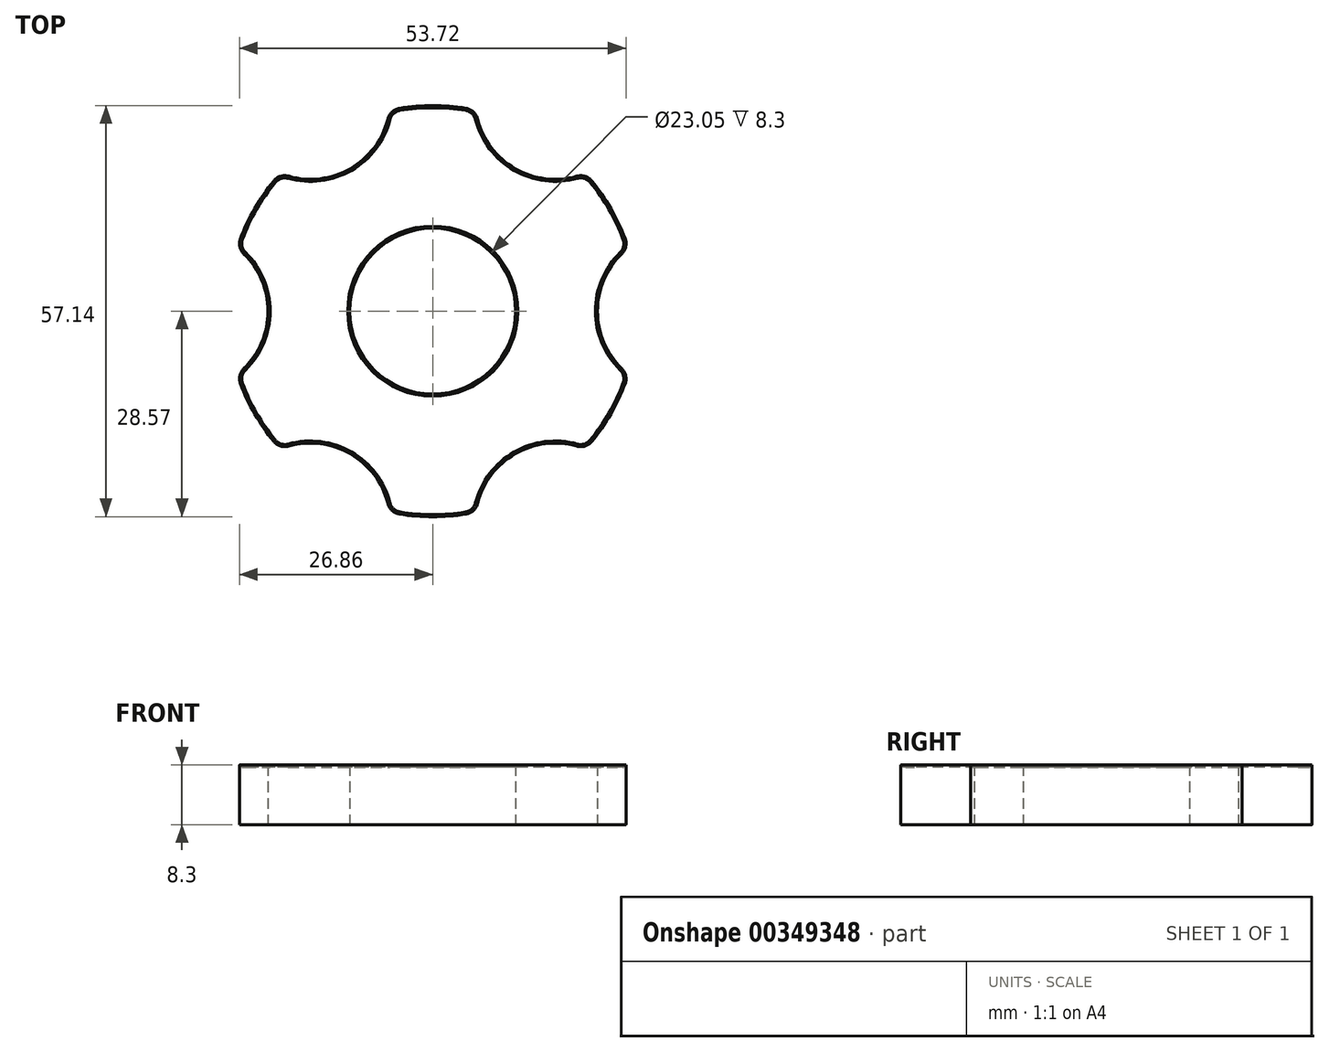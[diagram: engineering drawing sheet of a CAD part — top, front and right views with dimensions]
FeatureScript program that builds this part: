
annotation { "Feature Type Name" : "Feature", "Feature Type Description" : "" }
export const myFeature = defineFeature(function(context is Context, id is Id, definition is map)
    precondition{}
    {
        {
            var Q0;
            Q0=qCreatedBy(makeId("Top.planeOp"),FACE);
            var sketch = newSketch(context, id + "F0", { "sketchPlane" : qUnion([Q0])});
            skCircle(sketch, "E0", {"center": v(0, 0) * mm, "radius": 28.58 * mm});
            skCircle(sketch, "E1", {"center": v(0, 0) * mm, "radius": 11.53 * mm});
            skSolve(sketch);
        }
        {
            var Q0;
            Q0=makeQuery(id+"F0.imprint","IMPRINT",FACE,{"disambiguationData":[TD([[makeQuery(id+"F0.imprint","IMPRINT",EDGE,{"derivedFrom":sQuery(id+"F0.wireOp",EDGE,"E0")}),1.0]])]});
            extrude(context, id + "F1", {"entities" : qUnion([Q0]), "depth" : 8 * mm, "offsetDistance" : 25 * mm});
        }
        {
            var Q0;
            Q0=qCreatedBy(makeId("Top.planeOp"),FACE);
            var sketch = newSketch(context, id + "F2", { "sketchPlane" : qUnion([Q0])});
            skCircle(sketch, "E2", {"center": v(0, 0) * mm, "radius": 34.01 * mm});
            skCircle(sketch, "E3", {"center": v(-34.01, 0) * mm, "radius": 11.11 * mm});
            skCircle(sketch, "E4.1.0", {"center": v(-17, -29.45) * mm, "radius": 11.11 * mm});
            skCircle(sketch, "E4.2.0", {"center": v(17, -29.45) * mm, "radius": 11.11 * mm});
            skCircle(sketch, "E4.3.0", {"center": v(34.01, 0) * mm, "radius": 11.11 * mm});
            skCircle(sketch, "E4.4.0", {"center": v(17, 29.45) * mm, "radius": 11.11 * mm});
            skCircle(sketch, "E4.5.0", {"center": v(-17, 29.45) * mm, "radius": 11.11 * mm});
            skSolve(sketch);
        }
        {
            var Q0;
            {var subQ0=sQuery(id+"F2.wireOp",EDGE,"E4.2.0");var subQ1=sQuery(id+"F2.wireOp",EDGE,"E2");var subQ2=makeQuery(id+"F2.imprint","INTERSECT",VERTEX,{"disambiguationData":[OD(0.0)],"derivedFrom":[subQ1,subQ0]});Q0=makeQuery(id+"F2.imprint","IMPRINT",FACE,{"disambiguationData":[TD([[makeQuery(id+"F2.imprint","IMPRINT",EDGE,{"disambiguationData":[TD([[subQ2,-1.0]])],"derivedFrom":subQ1}),1.0]])]});}
            var Q1;
            {var subQ0=sQuery(id+"F2.wireOp",EDGE,"E4.1.0");var subQ1=sQuery(id+"F2.wireOp",EDGE,"E2");var subQ2=makeQuery(id+"F2.imprint","INTERSECT",VERTEX,{"disambiguationData":[OD(0.0)],"derivedFrom":[subQ1,subQ0]});Q1=makeQuery(id+"F2.imprint","IMPRINT",FACE,{"disambiguationData":[TD([[makeQuery(id+"F2.imprint","IMPRINT",EDGE,{"disambiguationData":[TD([[subQ2,-1.0]])],"derivedFrom":subQ1}),1.0]])]});}
            var Q2;
            {var subQ0=sQuery(id+"F2.wireOp",EDGE,"E3");var subQ1=sQuery(id+"F2.wireOp",EDGE,"E2");var subQ2=makeQuery(id+"F2.imprint","INTERSECT",VERTEX,{"disambiguationData":[OD(0.0)],"derivedFrom":[subQ1,subQ0]});Q2=makeQuery(id+"F2.imprint","IMPRINT",FACE,{"disambiguationData":[TD([[makeQuery(id+"F2.imprint","IMPRINT",EDGE,{"disambiguationData":[TD([[subQ2,-1.0]])],"derivedFrom":subQ1}),1.0]])]});}
            var Q3;
            {var subQ0=sQuery(id+"F2.wireOp",EDGE,"E4.5.0");var subQ1=sQuery(id+"F2.wireOp",EDGE,"E2");var subQ2=makeQuery(id+"F2.imprint","INTERSECT",VERTEX,{"disambiguationData":[OD(0.0)],"derivedFrom":[subQ1,subQ0]});Q3=makeQuery(id+"F2.imprint","IMPRINT",FACE,{"disambiguationData":[TD([[makeQuery(id+"F2.imprint","IMPRINT",EDGE,{"disambiguationData":[TD([[subQ2,-1.0]])],"derivedFrom":subQ1}),1.0]])]});}
            var Q4;
            {var subQ0=sQuery(id+"F2.wireOp",EDGE,"E4.4.0");var subQ1=sQuery(id+"F2.wireOp",EDGE,"E2");var subQ2=makeQuery(id+"F2.imprint","INTERSECT",VERTEX,{"disambiguationData":[OD(0.0)],"derivedFrom":[subQ1,subQ0]});Q4=makeQuery(id+"F2.imprint","IMPRINT",FACE,{"disambiguationData":[TD([[makeQuery(id+"F2.imprint","IMPRINT",EDGE,{"disambiguationData":[TD([[subQ2,-1.0]])],"derivedFrom":subQ1}),1.0]])]});}
            var Q5;
            {var subQ0=sQuery(id+"F2.wireOp",EDGE,"E4.3.0");var subQ1=sQuery(id+"F2.wireOp",EDGE,"E2");var subQ2=makeQuery(id+"F2.imprint","INTERSECT",VERTEX,{"disambiguationData":[OD(0.0)],"derivedFrom":[subQ1,subQ0]});Q5=makeQuery(id+"F2.imprint","IMPRINT",FACE,{"disambiguationData":[TD([[makeQuery(id+"F2.imprint","IMPRINT",EDGE,{"disambiguationData":[TD([[subQ2,1.0]])],"derivedFrom":subQ1}),1.0]])]});}
            extrude(context, id + "F3", {"entities" : qUnion([Q0, Q1, Q2, Q3, Q4, Q5]), "operationType" : NewBodyOperationType.REMOVE, "depth" : 25.4 * mm});
        }
        {
            var Q0;
            Q0=qCreatedBy(makeId("Top.planeOp"),FACE);
            var sketch = newSketch(context, id + "F4", { "sketchPlane" : qUnion([Q0])});
            skCircle(sketch, "E5", {"center": v(0, 22.86) * mm, "radius": 2.38 * mm});
            skCircle(sketch, "E6.1.0", {"center": v(-19.8, 11.43) * mm, "radius": 2.38 * mm});
            skCircle(sketch, "E6.2.0", {"center": v(-19.8, -11.43) * mm, "radius": 2.38 * mm});
            skCircle(sketch, "E6.3.0", {"center": v(0, -22.86) * mm, "radius": 2.38 * mm});
            skCircle(sketch, "E6.4.0", {"center": v(19.8, -11.43) * mm, "radius": 2.38 * mm});
            skCircle(sketch, "E6.5.0", {"center": v(19.8, 11.43) * mm, "radius": 2.38 * mm});
            skPoint(sketch, "E6.center", {"position": v(0, 0) * mm});
            skSolve(sketch);
        }
        {
            var Q0;
            Q0=makeQuery(id+"F3.boolean.opBoolean","INTERSECT",EDGE,{"disambiguationData":[OD(0.0)],"derivedFrom":[makeQuery(id+"F1.opExtrude","SWEPT_FACE",FACE,{"disambiguationData":[OSD([sQuery(id+"F0.wireOp",EDGE,"E0")])]}),makeQuery(id+"F3.opExtrude","SWEPT_FACE",FACE,{"disambiguationData":[OSD([sQuery(id+"F2.wireOp",EDGE,"E4.1.0")])]})]});
            var Q1;
            Q1=makeQuery(id+"F3.boolean.opBoolean","INTERSECT",EDGE,{"disambiguationData":[OD(0.0)],"derivedFrom":[makeQuery(id+"F1.opExtrude","SWEPT_FACE",FACE,{"disambiguationData":[OSD([sQuery(id+"F0.wireOp",EDGE,"E0")])]}),makeQuery(id+"F3.opExtrude","SWEPT_FACE",FACE,{"disambiguationData":[OSD([sQuery(id+"F2.wireOp",EDGE,"E3")])]})]});
            var Q2;
            Q2=makeQuery(id+"F3.boolean.opBoolean","INTERSECT",EDGE,{"disambiguationData":[OD(1.0)],"derivedFrom":[makeQuery(id+"F1.opExtrude","SWEPT_FACE",FACE,{"disambiguationData":[OSD([sQuery(id+"F0.wireOp",EDGE,"E0")])]}),makeQuery(id+"F3.opExtrude","SWEPT_FACE",FACE,{"disambiguationData":[OSD([sQuery(id+"F2.wireOp",EDGE,"E3")])]})]});
            var Q3;
            Q3=makeQuery(id+"F3.boolean.opBoolean","INTERSECT",EDGE,{"disambiguationData":[OD(0.0)],"derivedFrom":[makeQuery(id+"F1.opExtrude","SWEPT_FACE",FACE,{"disambiguationData":[OSD([sQuery(id+"F0.wireOp",EDGE,"E0")])]}),makeQuery(id+"F3.opExtrude","SWEPT_FACE",FACE,{"disambiguationData":[OSD([sQuery(id+"F2.wireOp",EDGE,"E4.5.0")])]})]});
            var Q4;
            Q4=makeQuery(id+"F3.boolean.opBoolean","INTERSECT",EDGE,{"disambiguationData":[OD(1.0)],"derivedFrom":[makeQuery(id+"F1.opExtrude","SWEPT_FACE",FACE,{"disambiguationData":[OSD([sQuery(id+"F0.wireOp",EDGE,"E0")])]}),makeQuery(id+"F3.opExtrude","SWEPT_FACE",FACE,{"disambiguationData":[OSD([sQuery(id+"F2.wireOp",EDGE,"E4.5.0")])]})]});
            var Q5;
            Q5=makeQuery(id+"F3.boolean.opBoolean","INTERSECT",EDGE,{"disambiguationData":[OD(1.0)],"derivedFrom":[makeQuery(id+"F1.opExtrude","SWEPT_FACE",FACE,{"disambiguationData":[OSD([sQuery(id+"F0.wireOp",EDGE,"E0")])]}),makeQuery(id+"F3.opExtrude","SWEPT_FACE",FACE,{"disambiguationData":[OSD([sQuery(id+"F2.wireOp",EDGE,"E4.4.0")])]})]});
            var Q6;
            Q6=makeQuery(id+"F3.boolean.opBoolean","INTERSECT",EDGE,{"disambiguationData":[OD(0.0)],"derivedFrom":[makeQuery(id+"F1.opExtrude","SWEPT_FACE",FACE,{"disambiguationData":[OSD([sQuery(id+"F0.wireOp",EDGE,"E0")])]}),makeQuery(id+"F3.opExtrude","SWEPT_FACE",FACE,{"disambiguationData":[OSD([sQuery(id+"F2.wireOp",EDGE,"E4.4.0")])]})]});
            var Q7;
            Q7=makeQuery(id+"F3.boolean.opBoolean","INTERSECT",EDGE,{"disambiguationData":[OD(1.0)],"derivedFrom":[makeQuery(id+"F1.opExtrude","SWEPT_FACE",FACE,{"disambiguationData":[OSD([sQuery(id+"F0.wireOp",EDGE,"E0")])]}),makeQuery(id+"F3.opExtrude","SWEPT_FACE",FACE,{"disambiguationData":[OSD([sQuery(id+"F2.wireOp",EDGE,"E4.3.0")])]})]});
            var Q8;
            Q8=makeQuery(id+"F3.boolean.opBoolean","INTERSECT",EDGE,{"disambiguationData":[OD(0.0)],"derivedFrom":[makeQuery(id+"F1.opExtrude","SWEPT_FACE",FACE,{"disambiguationData":[OSD([sQuery(id+"F0.wireOp",EDGE,"E0")])]}),makeQuery(id+"F3.opExtrude","SWEPT_FACE",FACE,{"disambiguationData":[OSD([sQuery(id+"F2.wireOp",EDGE,"E4.3.0")])]})]});
            var Q9;
            Q9=makeQuery(id+"F3.boolean.opBoolean","INTERSECT",EDGE,{"disambiguationData":[OD(1.0)],"derivedFrom":[makeQuery(id+"F1.opExtrude","SWEPT_FACE",FACE,{"disambiguationData":[OSD([sQuery(id+"F0.wireOp",EDGE,"E0")])]}),makeQuery(id+"F3.opExtrude","SWEPT_FACE",FACE,{"disambiguationData":[OSD([sQuery(id+"F2.wireOp",EDGE,"E4.2.0")])]})]});
            var Q10;
            Q10=makeQuery(id+"F3.boolean.opBoolean","INTERSECT",EDGE,{"disambiguationData":[OD(0.0)],"derivedFrom":[makeQuery(id+"F1.opExtrude","SWEPT_FACE",FACE,{"disambiguationData":[OSD([sQuery(id+"F0.wireOp",EDGE,"E0")])]}),makeQuery(id+"F3.opExtrude","SWEPT_FACE",FACE,{"disambiguationData":[OSD([sQuery(id+"F2.wireOp",EDGE,"E4.2.0")])]})]});
            var Q11;
            Q11=makeQuery(id+"F3.boolean.opBoolean","INTERSECT",EDGE,{"disambiguationData":[OD(1.0)],"derivedFrom":[makeQuery(id+"F1.opExtrude","SWEPT_FACE",FACE,{"disambiguationData":[OSD([sQuery(id+"F0.wireOp",EDGE,"E0")])]}),makeQuery(id+"F3.opExtrude","SWEPT_FACE",FACE,{"disambiguationData":[OSD([sQuery(id+"F2.wireOp",EDGE,"E4.1.0")])]})]});
            fillet(context, id + "F5", {"entities" : qUnion([Q0, Q1, Q2, Q3, Q4, Q5, Q6, Q7, Q8, Q9, Q10, Q11]), "radius" : 2 * mm, "tangentPropagation" : true, "allowEdgeOverflow" : false});
        }
        {
            var Q0;
            Q0=makeQuery(id+"F1.opExtrude","CAP_FACE",FACE,{"disambiguationData":[OSD([sQuery(id+"F0.wireOp",EDGE,"E0"),sQuery(id+"F0.wireOp",EDGE,"E1")])],"isStart":false});
            var sketch = newSketch(context, id + "F6", { "sketchPlane" : qUnion([Q0])});
            skArc(sketch, "E7.0.0", {"start": v(-26.73, -10.1) * mm, "mid": v(-24.75, -14.29) * mm, "end": v(-22.11, -18.1) * mm});
            skArc(sketch, "E7.0.1", {"start": v(-22.11, -18.1) * mm, "mid": v(-21.16, -18.74) * mm, "end": v(-20.02, -18.76) * mm});
            skArc(sketch, "E7.0.2", {"start": v(-20.02, -18.76) * mm, "mid": v(-11.45, -19.83) * mm, "end": v(-6.24, -26.72) * mm});
            skArc(sketch, "E7.0.3", {"start": v(-6.24, -26.72) * mm, "mid": v(-5.65, -27.7) * mm, "end": v(-4.62, -28.2) * mm});
            skArc(sketch, "E7.0.4", {"start": v(-4.62, -28.2) * mm, "mid": v(0, -28.58) * mm, "end": v(4.62, -28.2) * mm});
            skArc(sketch, "E7.0.5", {"start": v(4.62, -28.2) * mm, "mid": v(5.65, -27.7) * mm, "end": v(6.24, -26.72) * mm});
            skArc(sketch, "E7.0.6", {"start": v(6.24, -26.72) * mm, "mid": v(11.45, -19.83) * mm, "end": v(20.02, -18.76) * mm});
            skArc(sketch, "E7.0.7", {"start": v(20.02, -18.76) * mm, "mid": v(21.16, -18.74) * mm, "end": v(22.11, -18.1) * mm});
            skArc(sketch, "E7.0.8", {"start": v(22.11, -18.1) * mm, "mid": v(24.75, -14.29) * mm, "end": v(26.73, -10.1) * mm});
            skArc(sketch, "E7.0.9", {"start": v(26.73, -10.1) * mm, "mid": v(26.81, -8.96) * mm, "end": v(26.26, -7.96) * mm});
            skArc(sketch, "E7.0.10", {"start": v(26.26, -7.96) * mm, "mid": v(22.9, 0) * mm, "end": v(26.26, 7.96) * mm});
            skArc(sketch, "E7.0.11", {"start": v(26.26, 7.96) * mm, "mid": v(26.81, 8.96) * mm, "end": v(26.73, 10.1) * mm});
            skArc(sketch, "E7.0.12", {"start": v(26.73, 10.1) * mm, "mid": v(24.75, 14.29) * mm, "end": v(22.11, 18.1) * mm});
            skArc(sketch, "E7.0.13", {"start": v(22.11, 18.1) * mm, "mid": v(21.16, 18.74) * mm, "end": v(20.02, 18.76) * mm});
            skArc(sketch, "E7.0.14", {"start": v(20.02, 18.76) * mm, "mid": v(11.45, 19.83) * mm, "end": v(6.24, 26.72) * mm});
            skArc(sketch, "E7.0.15", {"start": v(6.24, 26.72) * mm, "mid": v(5.65, 27.7) * mm, "end": v(4.62, 28.2) * mm});
            skArc(sketch, "E7.0.16", {"start": v(4.62, 28.2) * mm, "mid": v(0, 28.58) * mm, "end": v(-4.62, 28.2) * mm});
            skArc(sketch, "E7.0.17", {"start": v(-4.62, 28.2) * mm, "mid": v(-5.65, 27.7) * mm, "end": v(-6.24, 26.72) * mm});
            skArc(sketch, "E7.0.18", {"start": v(-6.24, 26.72) * mm, "mid": v(-11.45, 19.83) * mm, "end": v(-20.02, 18.76) * mm});
            skArc(sketch, "E7.0.19", {"start": v(-20.02, 18.76) * mm, "mid": v(-21.16, 18.74) * mm, "end": v(-22.11, 18.1) * mm});
            skArc(sketch, "E7.0.20", {"start": v(-22.11, 18.1) * mm, "mid": v(-24.75, 14.29) * mm, "end": v(-26.73, 10.1) * mm});
            skArc(sketch, "E7.0.21", {"start": v(-26.73, 10.1) * mm, "mid": v(-26.81, 8.96) * mm, "end": v(-26.26, 7.96) * mm});
            skArc(sketch, "E7.0.22", {"start": v(-26.26, 7.96) * mm, "mid": v(-22.9, 0) * mm, "end": v(-26.26, -7.96) * mm});
            skArc(sketch, "E7.0.23", {"start": v(-26.26, -7.96) * mm, "mid": v(-26.81, -8.96) * mm, "end": v(-26.73, -10.1) * mm});
            skArc(sketch, "E8.0", {"start": v(-26.45, 10) * mm, "mid": v(-26.52, 9.02) * mm, "end": v(-26.05, 8.17) * mm});
            skArc(sketch, "E8.1", {"start": v(21.88, -17.91) * mm, "mid": v(24.49, -14.14) * mm, "end": v(26.45, -10) * mm});
            skArc(sketch, "E8.2", {"start": v(20.1, -18.47) * mm, "mid": v(21.07, -18.46) * mm, "end": v(21.88, -17.91) * mm});
            skArc(sketch, "E8.3", {"start": v(5.94, -26.64) * mm, "mid": v(11.3, -19.57) * mm, "end": v(20.1, -18.47) * mm});
            skArc(sketch, "E8.4", {"start": v(4.57, -27.9) * mm, "mid": v(5.45, -27.48) * mm, "end": v(5.94, -26.64) * mm});
            skArc(sketch, "E8.5", {"start": v(-4.57, -27.9) * mm, "mid": v(0, -28.28) * mm, "end": v(4.57, -27.9) * mm});
            skArc(sketch, "E8.6", {"start": v(-5.94, -26.64) * mm, "mid": v(-5.45, -27.48) * mm, "end": v(-4.57, -27.9) * mm});
            skArc(sketch, "E8.7", {"start": v(-26.05, -8.17) * mm, "mid": v(-26.52, -9.02) * mm, "end": v(-26.45, -10) * mm});
            skArc(sketch, "E8.8", {"start": v(-26.45, -10) * mm, "mid": v(-24.49, -14.14) * mm, "end": v(-21.88, -17.91) * mm});
            skArc(sketch, "E8.9", {"start": v(-21.88, -17.91) * mm, "mid": v(-21.07, -18.46) * mm, "end": v(-20.1, -18.47) * mm});
            skArc(sketch, "E8.10", {"start": v(-20.1, -18.47) * mm, "mid": v(-11.3, -19.57) * mm, "end": v(-5.94, -26.64) * mm});
            skArc(sketch, "E8.11", {"start": v(26.45, -10) * mm, "mid": v(26.52, -9.02) * mm, "end": v(26.05, -8.17) * mm});
            skArc(sketch, "E8.12", {"start": v(-26.05, 8.17) * mm, "mid": v(-22.6, 0) * mm, "end": v(-26.05, -8.17) * mm});
            skArc(sketch, "E8.13", {"start": v(26.05, -8.17) * mm, "mid": v(22.6, 0) * mm, "end": v(26.05, 8.17) * mm});
            skArc(sketch, "E8.14", {"start": v(26.05, 8.17) * mm, "mid": v(26.52, 9.02) * mm, "end": v(26.45, 10) * mm});
            skArc(sketch, "E8.15", {"start": v(26.45, 10) * mm, "mid": v(24.49, 14.14) * mm, "end": v(21.88, 17.91) * mm});
            skArc(sketch, "E8.16", {"start": v(21.88, 17.91) * mm, "mid": v(21.07, 18.46) * mm, "end": v(20.1, 18.47) * mm});
            skArc(sketch, "E8.17", {"start": v(20.1, 18.47) * mm, "mid": v(11.3, 19.57) * mm, "end": v(5.94, 26.64) * mm});
            skArc(sketch, "E8.18", {"start": v(5.94, 26.64) * mm, "mid": v(5.45, 27.48) * mm, "end": v(4.57, 27.9) * mm});
            skArc(sketch, "E8.19", {"start": v(4.57, 27.9) * mm, "mid": v(0, 28.28) * mm, "end": v(-4.57, 27.9) * mm});
            skArc(sketch, "E8.20", {"start": v(-4.57, 27.9) * mm, "mid": v(-5.45, 27.48) * mm, "end": v(-5.94, 26.64) * mm});
            skArc(sketch, "E8.21", {"start": v(-5.94, 26.64) * mm, "mid": v(-11.3, 19.57) * mm, "end": v(-20.1, 18.47) * mm});
            skArc(sketch, "E8.22", {"start": v(-20.1, 18.47) * mm, "mid": v(-21.07, 18.46) * mm, "end": v(-21.88, 17.91) * mm});
            skArc(sketch, "E8.23", {"start": v(-21.88, 17.91) * mm, "mid": v(-24.49, 14.14) * mm, "end": v(-26.45, 10) * mm});
            skCircle(sketch, "E9.0", {"center": v(0, 0) * mm, "radius": 11.83 * mm});
            skSolve(sketch);
        }
        {
            var Q0;
            Q0 = qSketchRegion(id + "F6", true);
            var Q1;
            Q1=makeQuery(id+"F6.imprint","IMPRINT",FACE,{"disambiguationData":[TD([[makeQuery(id+"F6.imprint","IMPRINT",EDGE,{"derivedFrom":sQuery(id+"F6.wireOp",EDGE,"E9.0")}),1.0]])]});
            extrude(context, id + "F7", {"entities" : qUnion([Q0, Q1]), "operationType" : NewBodyOperationType.ADD, "depth" : .3 * mm, "offsetDistance" : 25 * mm});
        }
    });
